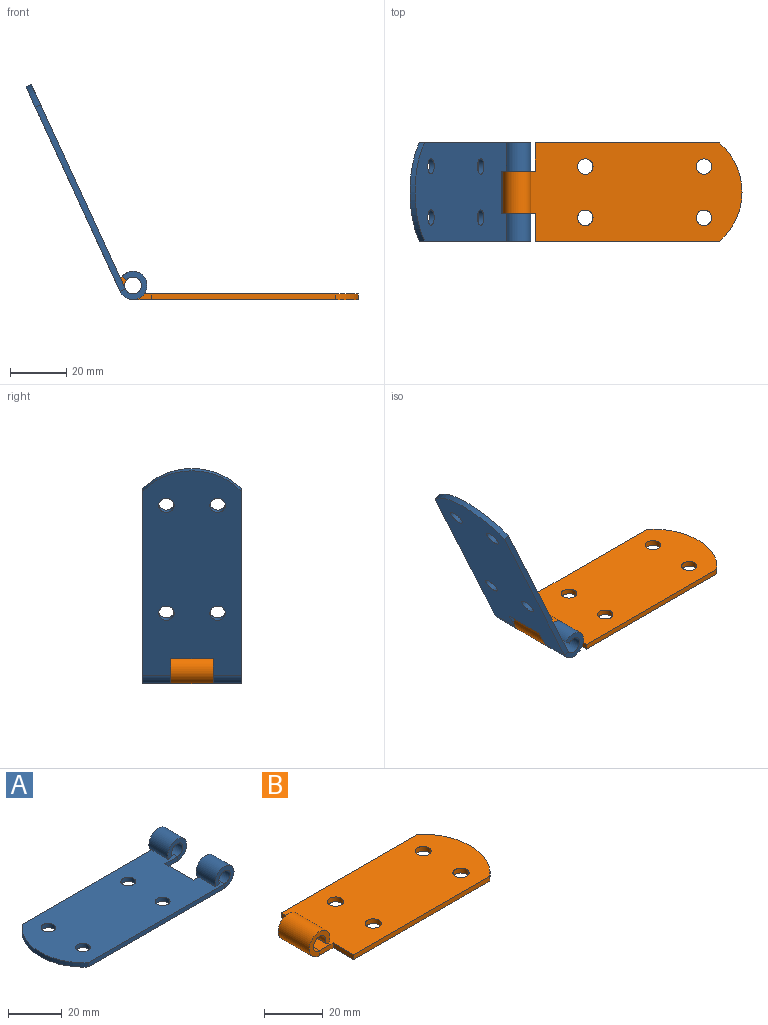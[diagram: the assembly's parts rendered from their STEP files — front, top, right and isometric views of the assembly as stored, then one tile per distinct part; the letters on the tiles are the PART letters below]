
ASSEMBLY  parts=2 mates=1
PART A: 22 faces, bbox 85x35x10 mm
  f0: plane 10x10mm, normal (0,1,0), area 41.2mm2, adj f1,f3,f4,f14
  f1: plane 10x1.81mm, normal (0.42,0,-0.91), area 20mm2, adj f0,f2,f3,f4
  f2: plane 10x10mm, normal (0,-1,0), area 41.2mm2, adj f1,f3,f4,f19
  f3: cylinder r=5mm len=10mm, axis (0,-1,0), area 257.5mm2, adj f0,f1,f2,f20
  f4: cylinder r=3mm len=10mm, axis (0,-1,0), area 154.5mm2, adj f0,f1,f2,f21
  f5: plane 10x10mm, normal (0,-1,0), area 41.2mm2, adj f7,f8,f9,f12
  f6: plane 10x10mm, normal (0,1,0), area 41.2mm2, adj f7,f8,f9,f11
  f7: plane 10x1.81mm, normal (0.42,0,-0.91), area 20mm2, adj f5,f6,f8,f9
  f8: cylinder r=5mm len=10mm, axis (0,-1,0), area 257.5mm2, adj f5,f6,f7,f20
  f9: cylinder r=3mm len=10mm, axis (0,-1,0), area 154.5mm2, adj f5,f6,f7,f21
  f10: plane 15x2mm, normal (1,0,0), area 30mm2, adj f11,f19,f20,f21
  f11: plane 6.5x2mm, normal (0,1,0), area 13mm2, adj f6,f10,f20,f21
  f12: plane 72x2mm, normal (0,-1,0), area 144mm2, adj f5,f13,f20,f21
  f13: cylinder r=23.14mm len=35mm, axis (0,0,-1), area 79.4mm2, adj f12,f14,f20,f21
  f14: plane 72x2mm, normal (0,1,0), area 144mm2, adj f0,f13,f20,f21
  f15: cylinder r=2.75mm len=5.5mm, axis (0,0,-1), area 34.6mm2, adj f20,f21
  f16: cylinder r=2.75mm len=5.5mm, axis (0,0,-1), area 34.6mm2, adj f20,f21
  f17: cylinder r=2.75mm len=5.5mm, axis (0,0,-1), area 34.6mm2, adj f20,f21
  f18: cylinder r=2.75mm len=5.5mm, axis (0,0,-1), area 34.6mm2, adj f20,f21
  f19: plane 6.5x2mm, normal (0,-1,0), area 13mm2, adj f2,f10,f20,f21
  f20: plane 80x35mm, normal (0,0,-1), area 2521.7mm2, adj f3,f8,f10,f11,f12,f13,f14,f15
  f21: plane 80x35mm, normal (0,0,1), area 2521.7mm2, adj f4,f9,f10,f11,f12,f13,f14,f15
PART B: 18 faces, bbox 85x35x10 mm
  f0: plane 10x10mm, normal (0,-1,0), area 41.2mm2, adj f1,f3,f4,f9
  f1: plane 15x1.81mm, normal (-0.42,0,-0.91), area 30mm2, adj f0,f2,f3,f4
  f2: plane 10x10mm, normal (0,1,0), area 41.2mm2, adj f1,f3,f4,f10
  f3: cylinder r=5mm len=15mm, axis (0,-1,0), area 386.3mm2, adj f0,f1,f2,f16
  f4: cylinder r=3mm len=15mm, axis (0,-1,0), area 231.8mm2, adj f0,f1,f2,f17
  f5: plane 65.5x2mm, normal (0,1,0), area 131mm2, adj f6,f15,f16,f17
  f6: cylinder r=23.14mm len=35mm, axis (0,0,-1), area 79.4mm2, adj f5,f7,f16,f17
  f7: plane 65.5x2mm, normal (0,-1,0), area 131mm2, adj f6,f8,f16,f17
  f8: plane 10x2mm, normal (-1,0,0), area 20mm2, adj f7,f9,f16,f17
  f9: plane 6.5x2mm, normal (0,-1,0), area 13mm2, adj f0,f8,f16,f17
  f10: plane 6.5x2mm, normal (0,1,0), area 13mm2, adj f2,f15,f16,f17
  f11: cylinder r=2.75mm len=5.5mm, axis (0,0,-1), area 34.6mm2, adj f16,f17
  f12: cylinder r=2.75mm len=5.5mm, axis (0,0,-1), area 34.6mm2, adj f16,f17
  f13: cylinder r=2.75mm len=5.5mm, axis (0,0,-1), area 34.6mm2, adj f16,f17
  f14: cylinder r=2.75mm len=5.5mm, axis (0,0,-1), area 34.6mm2, adj f16,f17
  f15: plane 10x2mm, normal (-1,0,0), area 20mm2, adj f5,f10,f16,f17
  f16: plane 80x35mm, normal (0,0,-1), area 2489.2mm2, adj f3,f5,f6,f7,f8,f9,f10,f11
  f17: plane 80x35mm, normal (0,0,1), area 2489.2mm2, adj f4,f5,f6,f7,f8,f9,f10,f11
PLACE A rot(axis=(0,1,0),65.3deg) t=(0,0,0)mm
PLACE B at identity fixed
MATE revolute B.f3 <-> A.f3  axis (0,-1,0) through (0,-7.5,0)mm
